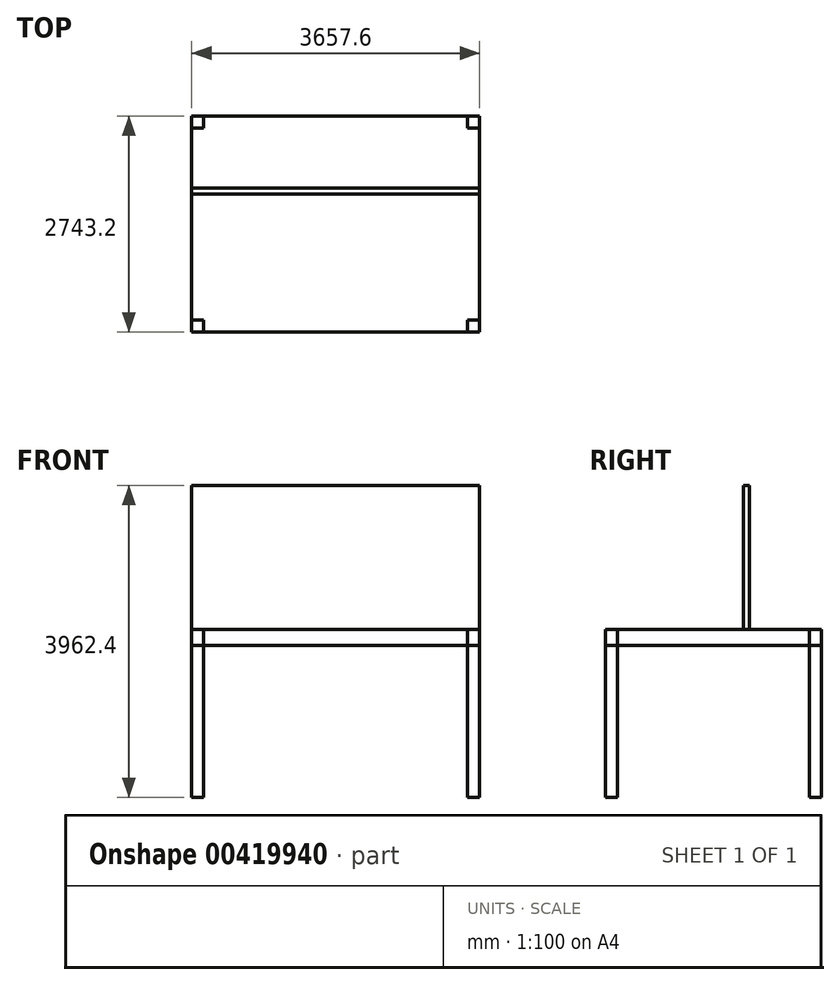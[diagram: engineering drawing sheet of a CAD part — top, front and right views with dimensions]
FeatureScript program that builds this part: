
annotation { "Feature Type Name" : "Feature", "Feature Type Description" : "" }
export const myFeature = defineFeature(function(context is Context, id is Id, definition is map)
    precondition{}
    {
        {
            var Q0;
            Q0=qCreatedBy(makeId("Top.planeOp"),FACE);
            var sketch = newSketch(context, id + "F0", { "sketchPlane" : qUnion([Q0])});
            skLineSegment(sketch, "E0.bottom", {"start": v(-1827.29, 978) * mm, "end": v(1830.31, 978) * mm});
            skLineSegment(sketch, "E0.top", {"start": v(-1827.29, -1765.2) * mm, "end": v(1830.31, -1765.2) * mm});
            skLineSegment(sketch, "E0.left", {"start": v(-1827.29, 978) * mm, "end": v(-1827.29, -1765.2) * mm});
            skLineSegment(sketch, "E0.right", {"start": v(1830.31, 978) * mm, "end": v(1830.31, -1765.2) * mm});
            skSolve(sketch);
        }
        {
            var Q0;
            Q0=makeQuery(id+"F0.imprint","IMPRINT",FACE,{"disambiguationData":[TD([[makeQuery(id+"F0.imprint","IMPRINT",EDGE,{"derivedFrom":sQuery(id+"F0.wireOp",EDGE,"E0.bottom")}),-1.0]])]});
            var sketch = newSketch(context, id + "F1", { "sketchPlane" : qUnion([Q0])});
            skLineSegment(sketch, "E1.bottom", {"start": v(-1827.29, 978) * mm, "end": v(-1674.89, 978) * mm});
            skLineSegment(sketch, "E1.top", {"start": v(-1827.29, 825.6) * mm, "end": v(-1674.89, 825.6) * mm});
            skLineSegment(sketch, "E1.left", {"start": v(-1827.29, 978) * mm, "end": v(-1827.29, 825.6) * mm});
            skLineSegment(sketch, "E1.right", {"start": v(-1674.89, 978) * mm, "end": v(-1674.89, 825.6) * mm});
            skLineSegment(sketch, "E2.bottom", {"start": v(-1827.29, -1612.8) * mm, "end": v(-1674.89, -1612.8) * mm});
            skLineSegment(sketch, "E2.top", {"start": v(-1827.29, -1765.2) * mm, "end": v(-1674.89, -1765.2) * mm});
            skLineSegment(sketch, "E2.left", {"start": v(-1827.29, -1612.8) * mm, "end": v(-1827.29, -1765.2) * mm});
            skLineSegment(sketch, "E2.right", {"start": v(-1674.89, -1612.8) * mm, "end": v(-1674.89, -1765.2) * mm});
            skLineSegment(sketch, "E3.bottom", {"start": v(1677.91, -1612.8) * mm, "end": v(1830.31, -1612.8) * mm});
            skLineSegment(sketch, "E3.top", {"start": v(1677.91, -1765.2) * mm, "end": v(1830.31, -1765.2) * mm});
            skLineSegment(sketch, "E3.left", {"start": v(1677.91, -1612.8) * mm, "end": v(1677.91, -1765.2) * mm});
            skLineSegment(sketch, "E3.right", {"start": v(1830.31, -1612.8) * mm, "end": v(1830.31, -1765.2) * mm});
            skLineSegment(sketch, "E4.bottom", {"start": v(1677.91, 978) * mm, "end": v(1830.31, 978) * mm});
            skLineSegment(sketch, "E4.top", {"start": v(1677.91, 825.6) * mm, "end": v(1830.31, 825.6) * mm});
            skLineSegment(sketch, "E4.left", {"start": v(1677.91, 978) * mm, "end": v(1677.91, 825.6) * mm});
            skLineSegment(sketch, "E4.right", {"start": v(1830.31, 978) * mm, "end": v(1830.31, 825.6) * mm});
            skSolve(sketch);
        }
        {
            var Q0;
            Q0 = qSketchRegion(id + "F1", true);
            extrude(context, id + "F2", {"entities" : qUnion([Q0]), "oppositeDirection" : true, "depth" : 2133.6 * mm, "offsetDistance" : 25.4 * mm});
        }
        {
            var Q0;
            Q0 = qSketchRegion(id + "F0", true);
            extrude(context, id + "F3", {"entities" : qUnion([Q0]), "oppositeDirection" : true, "depth" : 203.2 * mm, "offsetDistance" : 25.4 * mm});
        }
        {
            var Q0;
            Q0=makeQuery(id+"F3.opExtrude","CAP_FACE",FACE,{"disambiguationData":[OSD([sQuery(id+"F0.wireOp",EDGE,"E0.bottom"),sQuery(id+"F0.wireOp",EDGE,"E0.top"),sQuery(id+"F0.wireOp",EDGE,"E0.left"),sQuery(id+"F0.wireOp",EDGE,"E0.right")])],"isStart":true});
            var sketch = newSketch(context, id + "F4", { "sketchPlane" : qUnion([Q0])});
            skLineSegment(sketch, "E5.bottom", {"start": v(-1827.29, 63.6) * mm, "end": v(1830.31, 63.6) * mm});
            skLineSegment(sketch, "E5.top", {"start": v(-1827.29, -12.6) * mm, "end": v(1830.31, -12.6) * mm});
            skLineSegment(sketch, "E5.left", {"start": v(-1827.29, 63.6) * mm, "end": v(-1827.29, -12.6) * mm});
            skLineSegment(sketch, "E5.right", {"start": v(1830.31, 63.6) * mm, "end": v(1830.31, -12.6) * mm});
            skSolve(sketch);
        }
        {
            var Q0;
            Q0=makeQuery(id+"F4.imprint","IMPRINT",FACE,{"disambiguationData":[TD([[makeQuery(id+"F4.imprint","IMPRINT",EDGE,{"derivedFrom":sQuery(id+"F4.wireOp",EDGE,"E5.bottom")}),-1.0]])]});
            extrude(context, id + "F5", {"entities" : qUnion([Q0]), "operationType" : NewBodyOperationType.ADD, "depth" : 1828.8 * mm, "offsetDistance" : 25.4 * mm});
        }
        {
            var Q0;
            Q0 = qSketchRegion(id + "F4", true);
            extrude(context, id + "F6", {"entities" : qUnion([Q0]), "operationType" : NewBodyOperationType.ADD, "depth" : 25.4 * mm, "offsetDistance" : 25.4 * mm});
        }
        {
            var Q0;
            Q0=makeQuery(id+"F5.boolean.opBoolean","MERGE",FACE,{"derivedFrom":[makeQuery(id+"F3.opExtrude","SWEPT_FACE",FACE,{"disambiguationData":[OSD([sQuery(id+"F0.wireOp",EDGE,"E0.left")])]}),makeQuery(id+"F5.opExtrude","SWEPT_FACE",FACE,{"disambiguationData":[OSD([sQuery(id+"F4.wireOp",EDGE,"E5.left")])]})]});
            var sketch = newSketch(context, id + "F7", { "sketchPlane" : qUnion([Q0])});
            skLineSegment(sketch, "E6.bottom", {"start": v(-63.6, 0.25) * mm, "end": v(12.6, 0.25) * mm});
            skLineSegment(sketch, "E6.top", {"start": v(-63.6, 0) * mm, "end": v(12.6, 0) * mm});
            skLineSegment(sketch, "E6.left", {"start": v(-63.6, 0.25) * mm, "end": v(-63.6, 0) * mm});
            skLineSegment(sketch, "E6.right", {"start": v(12.6, 0.25) * mm, "end": v(12.6, 0) * mm});
            skSolve(sketch);
        }
        {
            var Q0;
            Q0 = qSketchRegion(id + "F7", true);
            extrude(context, id + "F8", {"entities" : qUnion([Q0]), "operationType" : NewBodyOperationType.REMOVE, "endBound" : BoundingType.UP_TO_NEXT, "oppositeDirection" : true, "depth" : 25.4 * mm, "offsetDistance" : 25.4 * mm});
        }
    });
